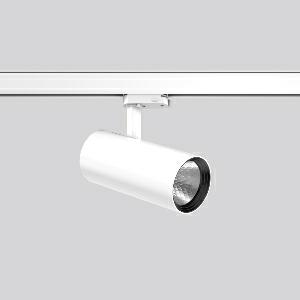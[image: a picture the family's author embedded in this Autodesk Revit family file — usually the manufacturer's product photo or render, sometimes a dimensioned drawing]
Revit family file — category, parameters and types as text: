
# Revit family: deecos_s_mini_742195_002_6d67
name_source: partatom
category: Lighting Fixtures
units: mm (PartAtom-declared; Revit-internal decimal feet)

## family parameters
Cut with Voids When Loaded = No
Host = Face
Light Source = No
Part Type = Normal
Room Calculation Point = No
Round Connector Dimension = Use Diameter
Shared = No

## types (1)
- DEECOS S mini (1 x LED Modul 930, 2500 lm, 3000)
    Apparent Load = 20 VA
    Approval mark = CE
    CIE Flux Codes = 100 100 100 100 100
    Color Rendering = 90
    Color Temperature = 3000
    Default Elevation = 1800 mm
    Description = Series: DEECOS S mini
LED surface-mounted projector in modern design with no visible cooling ribs. Housing: die-cast aluminium, powder-coated. Rotation range: 356°. Swivel range: 90°. Black plastic ring and recessed LED to prevent glare from the side. Optical assembly with reflector made of MIRO-Silver with 98% total light reflection for outstanding efficiency - can be changed without tools. Best colour rendering index Ra>90. With multi adaptor for 3-circuit tracks 230 V. Suitable for Track on ceiling, Wall track. High quality converter without flickering and stroboscopic effect. The following accessories can be mounted without use of tools: interchangeable lenses, decorative glasses, honeycomb louvre, clear and frosted diffusers, white interchangeable plastic ring. 
Colour: traffic white, matt (RAL 9016)
Diameter: 87 mm
Height: 214 mm
Lamp: LED
Socket: without socket
Colour temperature: 3000K
Colour rendering index (CRI): 92
System power: 20 W
Rated luminous flux: 2500 lm
Luminous efficiency: 125 lm/W
Control gear: Regulated power supply
Protection class: I
Type of protection: IP 20
    Height = 214 mm
    Lamp = 1 x LED Modul 930
    Lamp Light Flux = 2500 lm
    Lamp count = 1
    Length = 87 mm
    Lifetime = 50000 h
    Luminous efficacy = 125 lm/W
    Manufacturer = RZB
    ModVariant = No
    Model = 742195.002
    Mounting Place = Ceiling
    Mounting Type = Rail mounted
    Number of Poles = 1
    OnlyDefault = Yes
    Power Factor = 1
    Product Name = DEECOS S mini
    Product group = Track mounted projectors
    ProductGroupID = 301
    Protection Class = Protection class I
    Protection Degree = IP 20
    RLX_Detail_Level = 1
    RLX_Emergency_Light_Flux = 0 lm
    RLX_Emergency_Type = 0
    RLX_Emergency_Type_DB = No
    RlxData = <blob elided: 34777 chars, md5=eb77cee1>
    Socket = socket
    Standby Power = 0 W
    System Light Flux = 2500 lm
    System Power = 20 W
    Type Comments = Product without accessories
    Type Image = 741926.002.jpg
    URL = http://relux.com
    VarID = ---
    Voltage = 230 V
    Voltage Range = 220-240 V
    Weight = 0.00 kg
    Width = 0 mm  [stored 0 ft]

note: [stored X ft] marks values corroborated as IEEE doubles in the binary element streams (Revit-internal decimal feet)

## geometry (parser evidence)
native form markers: Blend x4, Sweep x12
no freeform markers — native parametric forms only
